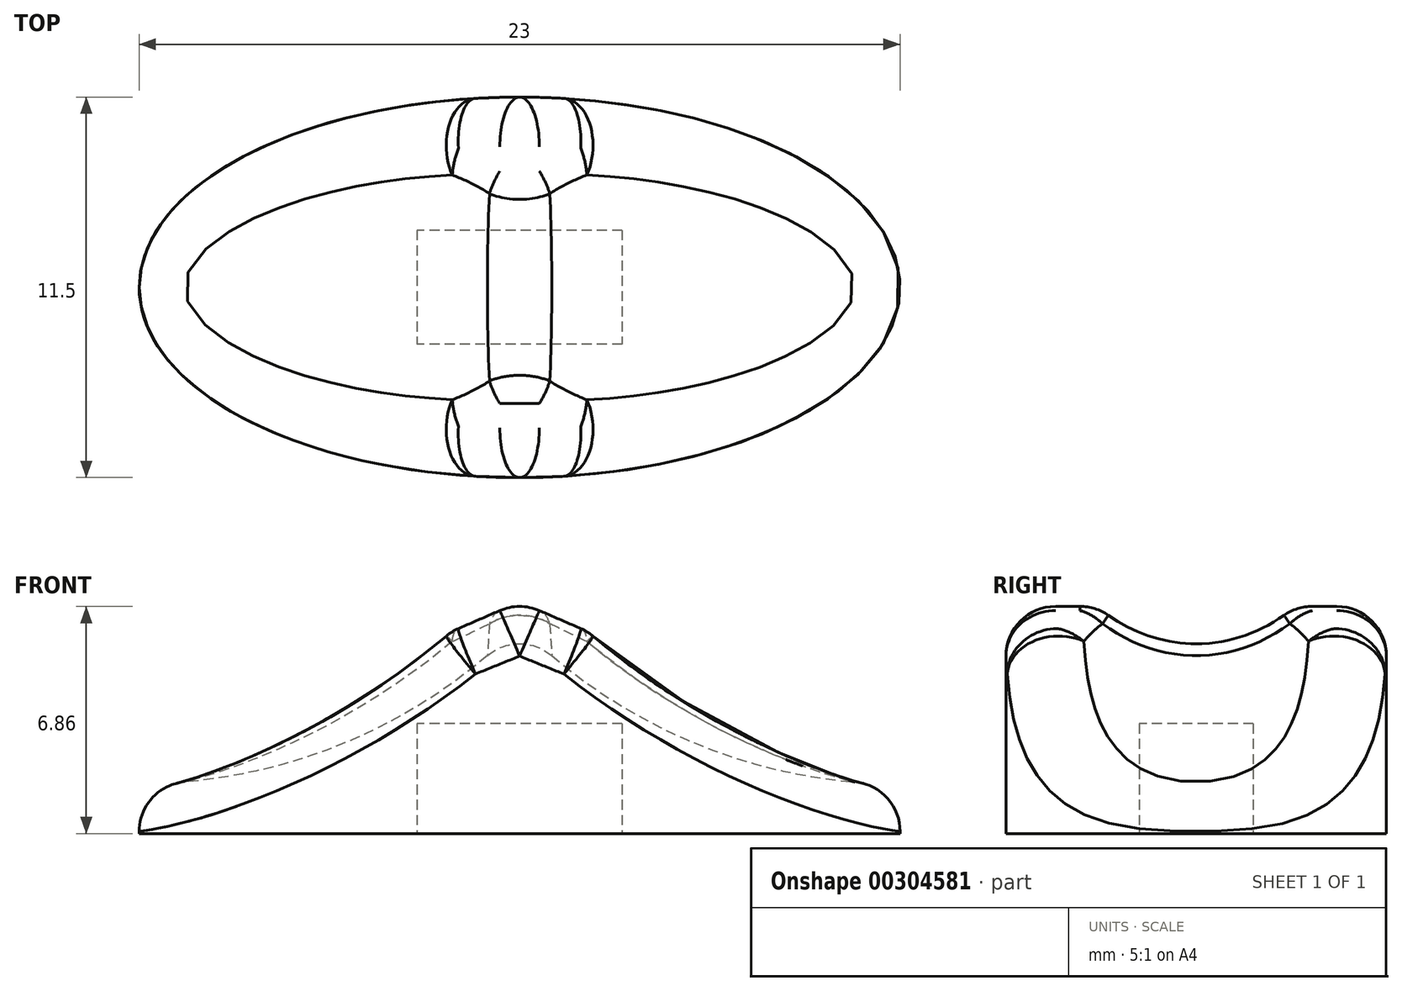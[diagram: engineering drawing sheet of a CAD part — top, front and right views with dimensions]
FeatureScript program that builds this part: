
annotation { "Feature Type Name" : "Feature", "Feature Type Description" : "" }
export const myFeature = defineFeature(function(context is Context, id is Id, definition is map)
    precondition{}
    {
        {
            var Q0;
            Q0=qCreatedBy(makeId("Front.planeOp"),FACE);
            var sketch = newSketch(context, id + "F0", { "sketchPlane" : qUnion([Q0])});
            skLineSegment(sketch, "E0.bottom", {"start": v(-11.5, 0) * mm, "end": v(11.5, 0) * mm});
            skLineSegment(sketch, "E0.top", {"start": v(-11.5, 2) * mm, "end": v(11.5, 2) * mm});
            skLineSegment(sketch, "E0.left", {"start": v(-11.5, 0) * mm, "end": v(-11.5, 2) * mm});
            skLineSegment(sketch, "E0.right", {"start": v(11.5, 0) * mm, "end": v(11.5, 2) * mm});
            skLineSegment(sketch, "E1", {"start": v(-11.5, 2) * mm, "end": v(0, 7) * mm});
            skLineSegment(sketch, "E2", {"start": v(0, 7) * mm, "end": v(11.5, 2) * mm});
            skArc(sketch, "E3", {"start": v(-11.5, 2) * mm, "mid": v(-5.23, 3.3) * mm, "end": v(0, 7) * mm});
            skArc(sketch, "E4", {"start": v(0, 7) * mm, "mid": v(5.23, 3.3) * mm, "end": v(11.5, 2) * mm});
            skCircle(sketch, "E5", {"center": v(-11.5, 17.73) * mm, "radius": 15.72 * mm});
            skCircle(sketch, "E6", {"center": v(11.5, 17.73) * mm, "radius": 15.72 * mm});
            skSolve(sketch);
        }
        {
            var Q0;
            {var subQ0=sQuery(id+"F0.wireOp",EDGE,"E1");Q0=makeQuery(id+"F0.imprint","IMPRINT",FACE,{"disambiguationData":[TD([[makeQuery(id+"F0.imprint","IMPRINT",EDGE,{"derivedFrom":subQ0}),-1.0]])]});}
            var Q1;
            {var subQ0=sQuery(id+"F0.wireOp",EDGE,"E0.top");Q1=makeQuery(id+"F0.imprint","IMPRINT",FACE,{"disambiguationData":[TD([[makeQuery(id+"F0.imprint","IMPRINT",EDGE,{"derivedFrom":subQ0}),1.0]])]});}
            var Q2;
            {var subQ0=sQuery(id+"F0.wireOp",EDGE,"E2");Q2=makeQuery(id+"F0.imprint","IMPRINT",FACE,{"disambiguationData":[TD([[makeQuery(id+"F0.imprint","IMPRINT",EDGE,{"derivedFrom":subQ0}),-1.0]])]});}
            var Q3;
            Q3=makeQuery(id+"F0.imprint","IMPRINT",FACE,{"disambiguationData":[TD([[makeQuery(id+"F0.imprint","IMPRINT",EDGE,{"derivedFrom":sQuery(id+"F0.wireOp",EDGE,"E0.bottom")}),1.0]])]});
            extrude(context, id + "F1", {"entities" : qUnion([Q0, Q1, Q2, Q3]), "endBound" : BoundingType.SYMMETRIC, "depth" : 11.5 * mm});
        }
        {
            var Q0;
            {var subQ0=sQuery(id+"F0.wireOp",EDGE,"E1");Q0=makeQuery(id+"F0.imprint","IMPRINT",FACE,{"disambiguationData":[TD([[makeQuery(id+"F0.imprint","IMPRINT",EDGE,{"derivedFrom":subQ0}),1.0]])]});}
            var Q1;
            {var subQ0=sQuery(id+"F0.wireOp",EDGE,"E6");var subQ1=sQuery(id+"F0.wireOp",EDGE,"E5");var subQ3=makeQuery(id+"F0.imprint","INTERSECT",VERTEX,{"derivedFrom":[subQ1,subQ0]});Q1=makeQuery(id+"F0.imprint","IMPRINT",FACE,{"disambiguationData":[TD([[makeQuery(id+"F0.imprint","IMPRINT",EDGE,{"disambiguationData":[TD([[subQ3,1.0]])],"derivedFrom":subQ1}),1.0]])]});}
            var Q2;
            {var subQ0=sQuery(id+"F0.wireOp",EDGE,"E1");Q2=makeQuery(id+"F0.imprint","IMPRINT",FACE,{"disambiguationData":[TD([[makeQuery(id+"F0.imprint","IMPRINT",EDGE,{"derivedFrom":subQ0}),-1.0]])]});}
            extrude(context, id + "F2", {"entities" : qUnion([Q0, Q1, Q2]), "endBound" : BoundingType.SYMMETRIC, "depth" : 11.5 * mm});
        }
        {
            var Q0;
            {var subQ0=sQuery(id+"F0.wireOp",EDGE,"E6");var subQ1=sQuery(id+"F0.wireOp",EDGE,"E5");var subQ3=makeQuery(id+"F0.imprint","INTERSECT",VERTEX,{"derivedFrom":[subQ1,subQ0]});Q0=makeQuery(id+"F0.imprint","IMPRINT",FACE,{"disambiguationData":[TD([[makeQuery(id+"F0.imprint","IMPRINT",EDGE,{"disambiguationData":[TD([[subQ3,1.0]])],"derivedFrom":subQ1}),1.0]])]});}
            var Q1;
            {var subQ0=sQuery(id+"F0.wireOp",EDGE,"E2");Q1=makeQuery(id+"F0.imprint","IMPRINT",FACE,{"disambiguationData":[TD([[makeQuery(id+"F0.imprint","IMPRINT",EDGE,{"derivedFrom":subQ0}),-1.0]])]});}
            var Q2;
            {var subQ0=sQuery(id+"F0.wireOp",EDGE,"E2");Q2=makeQuery(id+"F0.imprint","IMPRINT",FACE,{"disambiguationData":[TD([[makeQuery(id+"F0.imprint","IMPRINT",EDGE,{"derivedFrom":subQ0}),1.0]])]});}
            extrude(context, id + "F3", {"entities" : qUnion([Q0, Q1, Q2]), "endBound" : BoundingType.SYMMETRIC, "depth" : 11.5 * mm});
        }
        {
            var Q0;
            Q0=makeQuery(id+"F2.opExtrude","SWEPT_FACE",FACE,{"disambiguationData":[OSD([sQuery(id+"F0.wireOp",EDGE,"E5")])]});
            var Q1;
            Q1=makeQuery(id+"F3.opExtrude","SWEPT_FACE",FACE,{"disambiguationData":[OSD([sQuery(id+"F0.wireOp",EDGE,"E6")])]});
            fillet(context, id + "F4", {"entities" : qUnion([Q0, Q1]), "radius" : (11.5 / 2) * mm, "tangentPropagation" : true, "allowEdgeOverflow" : false});
        }
        {
            var Q0;
            Q0=makeQuery(id+"F2.opExtrude","SWEPT_BODY",BODY,{"disambiguationData":[OSD([sQuery(id+"F0.wireOp",EDGE,"E5")])]});
            var Q1;
            Q1=makeQuery(id+"F3.opExtrude","SWEPT_BODY",BODY,{"disambiguationData":[OSD([sQuery(id+"F0.wireOp",EDGE,"E6")])]});
            var Q2;
            Q2=makeQuery(id+"F1.opExtrude","SWEPT_BODY",BODY,{"disambiguationData":[OSD([sQuery(id+"F0.wireOp",EDGE,"E0.bottom"),sQuery(id+"F0.wireOp",EDGE,"E0.left"),sQuery(id+"F0.wireOp",EDGE,"E0.right"),sQuery(id+"F0.wireOp",EDGE,"E1"),sQuery(id+"F0.wireOp",EDGE,"E2")])]});
            booleanBodies(context, id + "F5", {"operationType" : BooleanOperationType.SUBTRACTION, "tools" : qUnion([Q0, Q1]), "targets" : qUnion([Q2]), "offset" : true, "offsetAll" : true, "offsetDistance" : .5 * mm});
        }
        {
            var Q0;
            Q0=makeQuery(id+"F1.opExtrude","SWEPT_FACE",FACE,{"disambiguationData":[OSD([sQuery(id+"F0.wireOp",EDGE,"E0.bottom")])]});
            var sketch = newSketch(context, id + "F6", { "sketchPlane" : qUnion([Q0])});
            skEllipse(sketch, "E7", {"center": v(0, 0) * mm, "majorRadius": 11.5 * mm, "minorRadius": 5.75 * mm, "majorAxis": v(-1, 0)});
            skLineSegment(sketch, "E8.0.0", {"start": v(-11.5, -5.75) * mm, "end": v(11.5, -5.75) * mm});
            skLineSegment(sketch, "E8.0.1", {"start": v(11.5, -5.75) * mm, "end": v(11.5, 5.75) * mm});
            skLineSegment(sketch, "E8.0.2", {"start": v(11.5, 5.75) * mm, "end": v(-11.5, 5.75) * mm});
            skLineSegment(sketch, "E8.0.3", {"start": v(-11.5, 5.75) * mm, "end": v(-11.5, -5.75) * mm});
            skSolve(sketch);
        }
        {
            var Q0;
            {var subQ0=sQuery(id+"F6.wireOp",EDGE,"E8.0.0");var subQ1=sQuery(id+"F6.wireOp",EDGE,"E7");var subQ2=makeQuery(id+"F6.imprint","INTERSECT",VERTEX,{"derivedFrom":[subQ1,subQ0]});Q0=makeQuery(id+"F6.imprint","IMPRINT",FACE,{"disambiguationData":[TD([[makeQuery(id+"F6.imprint","IMPRINT",EDGE,{"disambiguationData":[TD([[subQ2,1.0]])],"derivedFrom":subQ1}),-1.0]])]});}
            var Q1;
            {var subQ0=sQuery(id+"F6.wireOp",EDGE,"E8.0.3");var subQ1=sQuery(id+"F6.wireOp",EDGE,"E7");var subQ2=makeQuery(id+"F6.imprint","INTERSECT",VERTEX,{"derivedFrom":[subQ1,subQ0]});Q1=makeQuery(id+"F6.imprint","IMPRINT",FACE,{"disambiguationData":[TD([[makeQuery(id+"F6.imprint","IMPRINT",EDGE,{"disambiguationData":[TD([[subQ2,1.0]])],"derivedFrom":subQ1}),-1.0]])]});}
            var Q2;
            {var subQ0=sQuery(id+"F6.wireOp",EDGE,"E8.0.1");var subQ1=sQuery(id+"F6.wireOp",EDGE,"E7");var subQ2=makeQuery(id+"F6.imprint","INTERSECT",VERTEX,{"derivedFrom":[subQ1,subQ0]});Q2=makeQuery(id+"F6.imprint","IMPRINT",FACE,{"disambiguationData":[TD([[makeQuery(id+"F6.imprint","IMPRINT",EDGE,{"disambiguationData":[TD([[subQ2,-1.0]])],"derivedFrom":subQ1}),-1.0]])]});}
            var Q3;
            {var subQ0=sQuery(id+"F6.wireOp",EDGE,"E8.0.0");var subQ1=sQuery(id+"F6.wireOp",EDGE,"E7");var subQ2=makeQuery(id+"F6.imprint","INTERSECT",VERTEX,{"derivedFrom":[subQ1,subQ0]});Q3=makeQuery(id+"F6.imprint","IMPRINT",FACE,{"disambiguationData":[TD([[makeQuery(id+"F6.imprint","IMPRINT",EDGE,{"disambiguationData":[TD([[subQ2,-1.0]])],"derivedFrom":subQ1}),-1.0]])]});}
            extrude(context, id + "F7", {"entities" : qUnion([Q0, Q1, Q2, Q3]), "operationType" : NewBodyOperationType.REMOVE, "endBound" : BoundingType.THROUGH_ALL, "oppositeDirection" : true, "depth" : 25 * mm});
        }
        {
            var Q0;
            Q0=makeQuery(id+"F5.tempBoolean.opBoolean","COPY",FACE,{"derivedFrom":makeQuery(id+"F5.offsetTempBody.opPattern","COPY",FACE,{"derivedFrom":makeQuery(id+"F4.opFillet","BLEND_FACE",FACE,{"disambiguationData":[OSD([sQuery(id+"F0.wireOp",EDGE,"E6")])]}),"instanceName":"1"})});
            var Q1;
            Q1=makeQuery(id+"F5.tempBoolean.opBoolean","COPY",FACE,{"derivedFrom":makeQuery(id+"F5.offsetTempBody.opPattern","COPY",FACE,{"derivedFrom":makeQuery(id+"F4.opFillet","BLEND_FACE",FACE,{"disambiguationData":[OSD([sQuery(id+"F0.wireOp",EDGE,"E5")])]}),"instanceName":"1"})});
            var Q2;
            {var subQ0=sQuery(id+"F0.wireOp",EDGE,"E2");var subQ1=sQuery(id+"F0.wireOp",EDGE,"E0.left");var subQ2=sQuery(id+"F0.wireOp",EDGE,"E1");Q2=makeQuery(id+"F5.tempBoolean.opBoolean","SPLIT",FACE,{"disambiguationData":[TD([makeQuery(id+"F1.opExtrude","CAP_FACE",FACE,{"disambiguationData":[OSD([sQuery(id+"F0.wireOp",EDGE,"E0.bottom"),subQ1,sQuery(id+"F0.wireOp",EDGE,"E0.right"),subQ2,subQ0])],"isStart":false})])],"derivedFrom":makeQuery(id+"F1.opExtrude","SWEPT_FACE",FACE,{"disambiguationData":[OSD([subQ2])]})});}
            var Q3;
            Q3=makeQuery(id+"F5.tempBoolean.opBoolean","INTERSECT",EDGE,{"disambiguationData":[OD(1.0)],"derivedFrom":[makeQuery(id+"F1.opExtrude","SWEPT_FACE",FACE,{"disambiguationData":[OSD([sQuery(id+"F0.wireOp",EDGE,"E2")])]}),makeQuery(id+"F5.offsetTempBody.opPattern","COPY",FACE,{"derivedFrom":makeQuery(id+"F4.opFillet","BLEND_FACE",FACE,{"disambiguationData":[OSD([sQuery(id+"F0.wireOp",EDGE,"E6")])]}),"instanceName":"1"})]});
            var Q4;
            {var subQ0=sQuery(id+"F0.wireOp",EDGE,"E1");var subQ1=sQuery(id+"F0.wireOp",EDGE,"E0.right");var subQ2=sQuery(id+"F0.wireOp",EDGE,"E2");Q4=makeQuery(id+"F5.tempBoolean.opBoolean","SPLIT",FACE,{"disambiguationData":[TD([makeQuery(id+"F1.opExtrude","CAP_FACE",FACE,{"disambiguationData":[OSD([sQuery(id+"F0.wireOp",EDGE,"E0.bottom"),sQuery(id+"F0.wireOp",EDGE,"E0.left"),subQ1,subQ0,subQ2])],"isStart":true})])],"derivedFrom":makeQuery(id+"F1.opExtrude","SWEPT_FACE",FACE,{"disambiguationData":[OSD([subQ2])]})});}
            var Q5;
            {var subQ0=sQuery(id+"F0.wireOp",EDGE,"E0.left");var subQ1=sQuery(id+"F0.wireOp",EDGE,"E2");var subQ2=sQuery(id+"F0.wireOp",EDGE,"E1");Q5=makeQuery(id+"F5.tempBoolean.opBoolean","SPLIT",FACE,{"disambiguationData":[TD([makeQuery(id+"F1.opExtrude","CAP_FACE",FACE,{"disambiguationData":[OSD([sQuery(id+"F0.wireOp",EDGE,"E0.bottom"),subQ0,sQuery(id+"F0.wireOp",EDGE,"E0.right"),subQ2,subQ1])],"isStart":true})])],"derivedFrom":makeQuery(id+"F1.opExtrude","SWEPT_FACE",FACE,{"disambiguationData":[OSD([subQ2])]})});}
            var Q6;
            {var subQ0=sQuery(id+"F0.wireOp",EDGE,"E1");var subQ1=sQuery(id+"F0.wireOp",EDGE,"E0.right");var subQ2=sQuery(id+"F0.wireOp",EDGE,"E2");Q6=makeQuery(id+"F5.tempBoolean.opBoolean","SPLIT",FACE,{"disambiguationData":[TD([makeQuery(id+"F1.opExtrude","CAP_FACE",FACE,{"disambiguationData":[OSD([sQuery(id+"F0.wireOp",EDGE,"E0.bottom"),sQuery(id+"F0.wireOp",EDGE,"E0.left"),subQ1,subQ0,subQ2])],"isStart":false})])],"derivedFrom":makeQuery(id+"F1.opExtrude","SWEPT_FACE",FACE,{"disambiguationData":[OSD([subQ2])]})});}
            fillet(context, id + "F8", {"entities" : qUnion([Q0, Q1, Q2, Q3, Q4, Q5, Q6]), "radius" : 1.5 * mm, "tangentPropagation" : true, "allowEdgeOverflow" : false});
        }
        {
            var Q0;
            Q0=makeQuery(id+"F1.opExtrude","SWEPT_FACE",FACE,{"disambiguationData":[OSD([sQuery(id+"F0.wireOp",EDGE,"E0.bottom")])]});
            var sketch = newSketch(context, id + "F9", { "sketchPlane" : qUnion([Q0])});
            skLineSegment(sketch, "E9.bottom", {"start": v(3, -1.62) * mm, "end": v(-3, -1.63) * mm});
            skLineSegment(sketch, "E9.top", {"start": v(3, 1.63) * mm, "end": v(-3, 1.62) * mm});
            skLineSegment(sketch, "E9.left", {"start": v(3, -1.62) * mm, "end": v(3, 1.63) * mm});
            skLineSegment(sketch, "E9.right", {"start": v(-3, -1.63) * mm, "end": v(-3, 1.62) * mm});
            skPoint(sketch, "E9.middle", {"position": v(0, 0) * mm});
            skLineSegment(sketch, "E10.0", {"start": v(3.1, -1.72) * mm, "end": v(3.1, 1.73) * mm});
            skLineSegment(sketch, "E10.1", {"start": v(3.1, -1.73) * mm, "end": v(-3.1, -1.73) * mm});
            skLineSegment(sketch, "E10.2", {"start": v(-3.1, -1.73) * mm, "end": v(-3.1, 1.72) * mm});
            skLineSegment(sketch, "E10.3", {"start": v(3.1, 1.73) * mm, "end": v(-3.1, 1.73) * mm});
            skSolve(sketch);
        }
        {
            var Q0;
            Q0=makeQuery(id+"F9.imprint","IMPRINT",FACE,{"disambiguationData":[TD([[makeQuery(id+"F9.imprint","IMPRINT",EDGE,{"derivedFrom":sQuery(id+"F9.wireOp",EDGE,"E9.bottom")}),1.0]])]});
            var Q1;
            Q1=makeQuery(id+"F9.imprint","IMPRINT",FACE,{"disambiguationData":[TD([[makeQuery(id+"F9.imprint","IMPRINT",EDGE,{"derivedFrom":sQuery(id+"F9.wireOp",EDGE,"E9.bottom")}),-1.0]])]});
            extrude(context, id + "F10", {"entities" : qUnion([Q0, Q1]), "operationType" : NewBodyOperationType.REMOVE, "oppositeDirection" : true, "depth" : 3.32 * mm});
        }
    });
